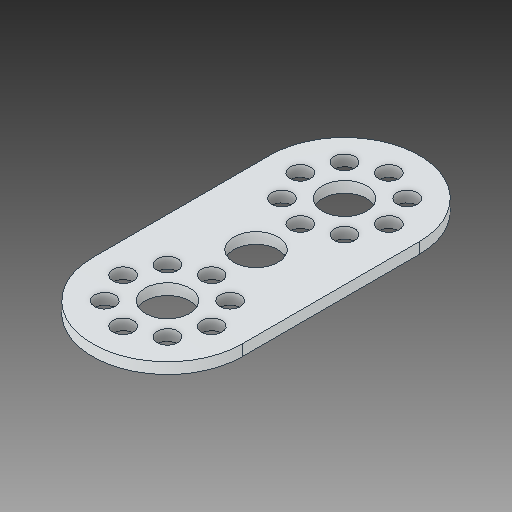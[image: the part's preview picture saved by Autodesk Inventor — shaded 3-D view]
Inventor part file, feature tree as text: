
AUTODESK INVENTOR PART (.ipt)
format: ipt  version: 2019 (Build 230136000, 136)  size: 156,672 bytes
history: native  units: in
note: dims shown in document units (in); Inventor stores cm internally (conversion verified against a paired STEP export)
features: extrude x1
ambient origin geometry x8: Origin, YZ Plane, XZ Plane, XY Plane, X Axis, Y Axis, Z Axis, Center Point
bodies: Solid1 (feature_tree)
feature tree (1):
  extrude  "Extrude2"  [1 undecoded]
note: 1 required parameter value undecoded (feature->parameter linkage not recoverable at this tier; creation-order binding heuristic only, values carry confidence <= 0.55)
